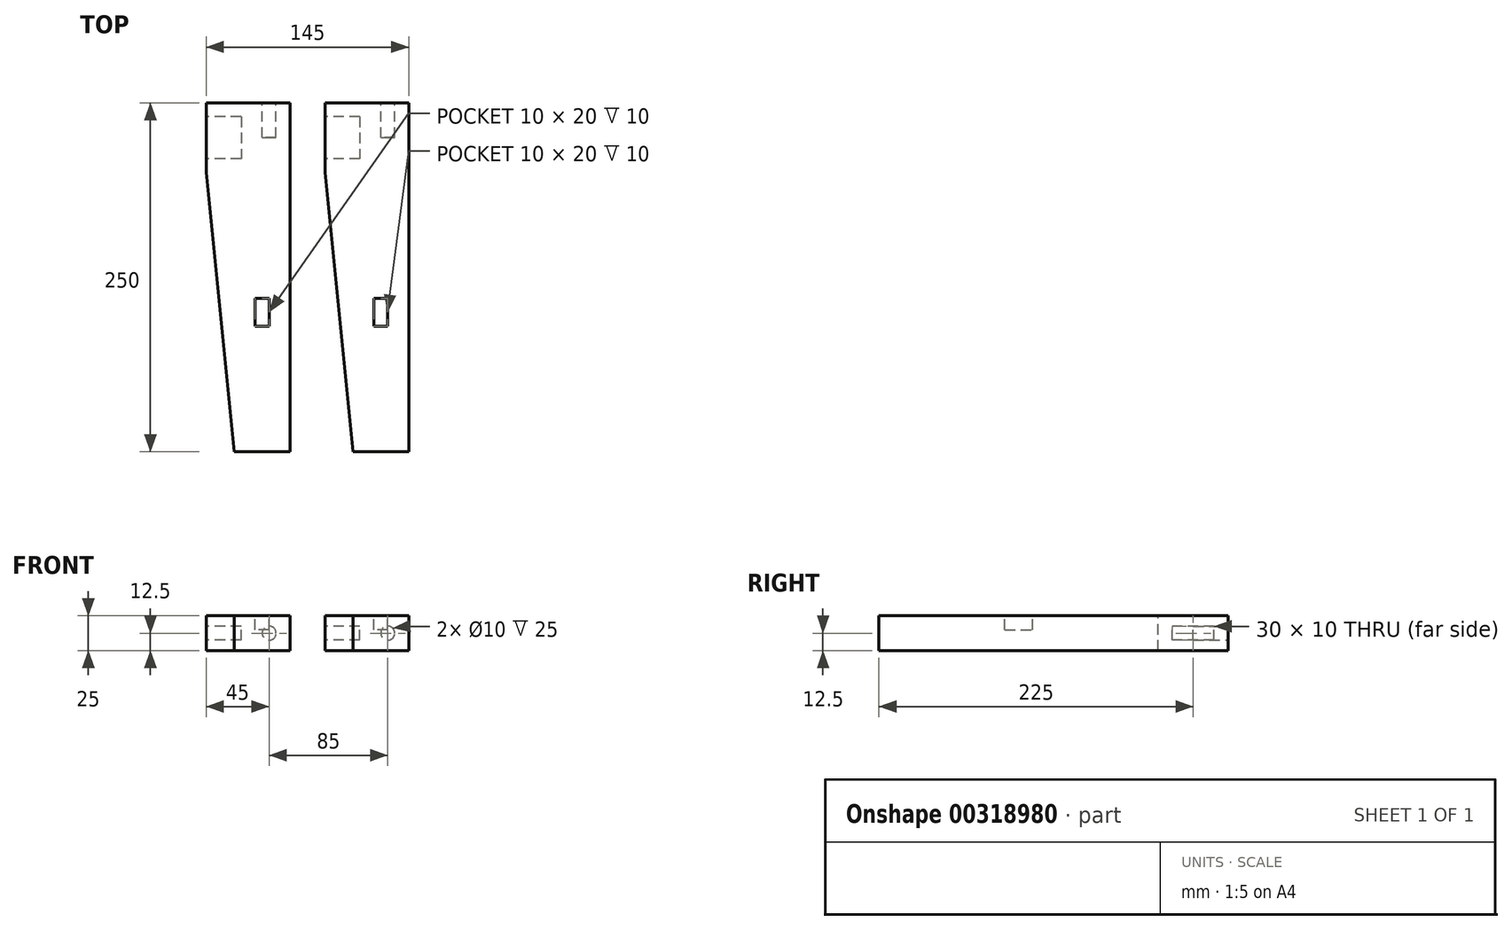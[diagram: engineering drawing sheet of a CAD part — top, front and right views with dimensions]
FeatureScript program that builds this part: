
annotation { "Feature Type Name" : "Feature", "Feature Type Description" : "" }
export const myFeature = defineFeature(function(context is Context, id is Id, definition is map)
    precondition{}
    {
        {
            var Q0;
            Q0=qCreatedBy(makeId("Top.planeOp"),FACE);
            var sketch = newSketch(context, id + "F0", { "sketchPlane" : qUnion([Q0])});
            skLineSegment(sketch, "E0.bottom", {"start": v(30, 125) * mm, "end": v(-30, 125) * mm});
            skLineSegment(sketch, "E0.left", {"start": v(30, 125) * mm, "end": v(30, -125) * mm});
            skPoint(sketch, "E0.middle", {"position": v(0, 0) * mm});
            skLineSegment(sketch, "E1", {"start": v(-30, 125) * mm, "end": v(-30, 75) * mm});
            skLineSegment(sketch, "E2", {"start": v(-30, 75) * mm, "end": v(-10, -125) * mm});
            skLineSegment(sketch, "E3", {"start": v(30, -125) * mm, "end": v(-10, -125) * mm});
            skSolve(sketch);
        }
        {
            var Q0;
            Q0=qSketchRegion(id+"F0",true);
            extrude(context, id + "F1", {"entities" : qUnion([Q0]), "depth" : 25 * mm});
        }
        {
            var Q0;
            Q0=makeQuery(id+"F1.opExtrude","SWEPT_FACE",FACE,{"disambiguationData":[OSD([sQuery(id+"F0.wireOp",EDGE,"E1")])]});
            var sketch = newSketch(context, id + "F2", { "sketchPlane" : qUnion([Q0])});
            skLineSegment(sketch, "E4", {"start": v(-125, 17.5) * mm, "end": v(-115, 17.5) * mm, "construction": true});
            skLineSegment(sketch, "E5", {"start": v(-115, 17.5) * mm, "end": v(-115, 25) * mm, "construction": true});
            skLineSegment(sketch, "E6.bottom", {"start": v(-115, 17.5) * mm, "end": v(-85, 17.5) * mm});
            skLineSegment(sketch, "E6.top", {"start": v(-115, 7.5) * mm, "end": v(-85, 7.5) * mm});
            skLineSegment(sketch, "E6.left", {"start": v(-115, 17.5) * mm, "end": v(-115, 7.5) * mm});
            skLineSegment(sketch, "E6.right", {"start": v(-85, 17.5) * mm, "end": v(-85, 7.5) * mm});
            skSolve(sketch);
        }
        {
            var Q0;
            Q0=qSketchRegion(id+"F2",true);
            extrude(context, id + "F3", {"entities" : qUnion([Q0]), "operationType" : NewBodyOperationType.REMOVE, "oppositeDirection" : true, "depth" : 25 * mm});
        }
        {
            var Q0;
            Q0=makeQuery(id+"F1.opExtrude","SWEPT_FACE",FACE,{"disambiguationData":[OSD([sQuery(id+"F0.wireOp",EDGE,"E0.bottom")])]});
            var sketch = newSketch(context, id + "F4", { "sketchPlane" : qUnion([Q0])});
            skLineSegment(sketch, "E7", {"start": v(-30, 12.5) * mm, "end": v(-15, 12.5) * mm, "construction": true});
            skLineSegment(sketch, "E8", {"start": v(-15, 12.5) * mm, "end": v(30, 12.5) * mm, "construction": true});
            skCircle(sketch, "E9", {"center": v(-15, 12.5) * mm, "radius": 5 * mm});
            skSolve(sketch);
        }
        {
            var Q0;
            Q0=qSketchRegion(id+"F4",true);
            extrude(context, id + "F5", {"entities" : qUnion([Q0]), "operationType" : NewBodyOperationType.REMOVE, "oppositeDirection" : true, "depth" : 25 * mm});
        }
        {
            var Q0;
            Q0=makeQuery(id+"F1.opExtrude","CAP_FACE",FACE,{"disambiguationData":[OSD([sQuery(id+"F0.wireOp",EDGE,"E0.bottom"),sQuery(id+"F0.wireOp",EDGE,"E0.left"),sQuery(id+"F0.wireOp",EDGE,"E1"),sQuery(id+"F0.wireOp",EDGE,"E2"),sQuery(id+"F0.wireOp",EDGE,"E3")])],"isStart":true});
            var sketch = newSketch(context, id + "F6", { "sketchPlane" : qUnion([Q0])});
            skLineSegment(sketch, "E10", {"start": v(15, 125) * mm, "end": v(15, 35) * mm, "construction": true});
            skLineSegment(sketch, "E11", {"start": v(15, 35) * mm, "end": v(30, 35) * mm, "construction": true});
            skLineSegment(sketch, "E12.bottom", {"start": v(15, 35) * mm, "end": v(5, 35) * mm});
            skLineSegment(sketch, "E12.top", {"start": v(15, 15) * mm, "end": v(5, 15) * mm});
            skLineSegment(sketch, "E12.left", {"start": v(15, 35) * mm, "end": v(15, 15) * mm});
            skLineSegment(sketch, "E12.right", {"start": v(5, 35) * mm, "end": v(5, 15) * mm});
            skSolve(sketch);
        }
        {
            var Q0;
            Q0=qSketchRegion(id+"F6",true);
            extrude(context, id + "F7", {"entities" : qUnion([Q0]), "operationType" : NewBodyOperationType.REMOVE, "oppositeDirection" : true, "depth" : 10 * mm});
        }
        {
            var Q0;
            Q0=qCreatedBy(makeId("Top.planeOp"),FACE);
            cPlane(context, id + "F8", {"entities" : qUnion([Q0]), "cplaneType" : CPlaneType.OFFSET, "offset" : 65 * mm, "oppositeDirection" : true, "width" : 150 * mm, "height" : 150 * mm});
        }
        {
            var Q0;
            Q0=makeQuery(id+"F1.opExtrude","SWEPT_BODY",BODY,{"disambiguationData":[OSD([sQuery(id+"F0.wireOp",EDGE,"E0.bottom"),sQuery(id+"F0.wireOp",EDGE,"E0.left"),sQuery(id+"F0.wireOp",EDGE,"E1"),sQuery(id+"F0.wireOp",EDGE,"E2"),sQuery(id+"F0.wireOp",EDGE,"E3")])]});
            var Q1;
            Q1=qCreatedBy(id+"F8.planeOp",FACE);
            mirror(context, id + "F9", {"entities" : qUnion([Q0]), "mirrorPlane" : qUnion([Q1])});
        }
        {
            var Q0;
            Q0=makeQuery(id+"F1.opExtrude","SWEPT_BODY",BODY,{"disambiguationData":[OSD([sQuery(id+"F0.wireOp",EDGE,"E0.bottom"),sQuery(id+"F0.wireOp",EDGE,"E0.left"),sQuery(id+"F0.wireOp",EDGE,"E1"),sQuery(id+"F0.wireOp",EDGE,"E2"),sQuery(id+"F0.wireOp",EDGE,"E3")])]});
            deleteBodies(context, id + "F10", {"entities" : qUnion([Q0])});
        }
        {
            var Q0;
            Q0=makeQuery(id+"F9.opPattern","COPY",BODY,{"derivedFrom":makeQuery(id+"F1.opExtrude","SWEPT_BODY",BODY,{"disambiguationData":[OSD([sQuery(id+"F0.wireOp",EDGE,"E0.bottom"),sQuery(id+"F0.wireOp",EDGE,"E0.left"),sQuery(id+"F0.wireOp",EDGE,"E1"),sQuery(id+"F0.wireOp",EDGE,"E2"),sQuery(id+"F0.wireOp",EDGE,"E3")])]}),"instanceName":"1"});
            transform(context, id + "F11", {"entities" : qUnion([Q0]), "transformType" : TransformType.COPY});
        }
        {
            var Q0;
            Q0=makeQuery(id+"F11.opPattern","COPY",BODY,{"derivedFrom":makeQuery(id+"F9.opPattern","COPY",BODY,{"derivedFrom":makeQuery(id+"F1.opExtrude","SWEPT_BODY",BODY,{"disambiguationData":[OSD([sQuery(id+"F0.wireOp",EDGE,"E0.bottom"),sQuery(id+"F0.wireOp",EDGE,"E0.left"),sQuery(id+"F0.wireOp",EDGE,"E1"),sQuery(id+"F0.wireOp",EDGE,"E2"),sQuery(id+"F0.wireOp",EDGE,"E3")])]}),"instanceName":"1"}),"instanceName":"1"});
            transform(context, id + "F12", {"entities" : qUnion([Q0]), "transformType" : TransformType.TRANSLATION_3D, "dx" : 85 * mm, "dy" : 0 * mm, "dz" : 0 * mm, "makeCopy" : false});
        }
    });
